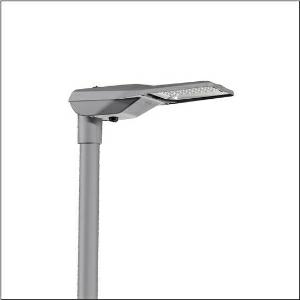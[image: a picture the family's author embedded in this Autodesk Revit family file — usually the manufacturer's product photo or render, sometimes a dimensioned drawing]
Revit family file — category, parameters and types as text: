
# Revit family: streetlight_sl_21_iq_mini___st1_0a_5xe2d21y08jb_5dbb
name_source: partatom
category: Lighting Fixtures
units: mm (PartAtom-declared; Revit-internal decimal feet)

## family parameters
Cut with Voids When Loaded = No
Host = Face
Light Source = No
Part Type = Normal
Room Calculation Point = No
Round Connector Dimension = Use Diameter
Shared = No

## types (1)
- --- (1 x LED, 9000 lm, 72.5 W, 2200K)
    Apparent Load = 73 VA
    CIE Flux Codes = 40 73 97 100 100
    Color Rendering = 70
    Color Temperature = 2200K
    Default Elevation = 1800 mm
    Description = Streetlight SL 21 iQ mini, mast luminaire, primary light control with lens, of PMMA, primary optical cover: cover, of toughened safety glass, transparent, light distribution: ST1.0a, light emission: direct distribution, primary light characteristic: asymmetric, installation type: post-top, side-entry, LED, High Power LED, rated luminous flux: 9.000lm, luminous efficacy: 124lm/W, light colour: 722, colour temperature: 2200K, control gear: iQ-Street Remote, D4i with power reduction, control: pre-setting: logarithmic dimming characteristic, Street-Remote, Auto-Match, Temp-Guard, Lumen-Switch, Night-Set, Smart-Wire, Light-Fading, Desk-Remote (wireless, voltage-free reading and setting of iQ features in the workshop via application-optimized NFC function/RFID function), optimised constant luminous flux control (CLO 2.0), mains connection: 220..240V, AC, 50/60Hz, start of lifetime: 73W, end of service life: 76W, reduction: 33W, luminaire housing, of diecast aluminium, powder-coated, Siteco® metallic grey (DB 702S), corrosivity category C5 mid according to DIN EN ISO 12944, please order mast flange separately, inclination adjustable: 0°, 5°, 10°, 15°, sealing non-destructively replaceable, multi-level sealing system, length: 628mm, width: 235mm, height: 110mm, mast flange for spigot size: 42mm (side-entry): 5XC10008XM4, 60/48mm (side-entry/post-top): 5XC10108XM2, 76/60mm (side-entry/post-top): 5XC10108XM1, mounting height: 4..8m, Smart Interface below and above, protection rating (complete): IP66, insulation class (complete): insulation class II (safety insulation), certification: CE, ENEC, ENEC+, VDE, impact resistance: IK10, permissible operating ambient temperature for outdoor applications: -40..+50°C, standard-compliant lighting for roads and squares, packaging unit: 1 piece

Light Distribution: ST1.0a
    Height = 110 mm
    Lamp = 1 x LED
    Lamp Light Flux = 9000 lm
    Lamp Power = 72.5 W
    Lamp count = 1
    Length = 625 mm
    Luminous efficacy = 124 lm/W
    Manufacturer = Siteco
    ModVariant = No
    Model = 5XE2D21Y08JB
    Number of Poles = 1
    OnlyDefault = Yes
    Power Factor = 1
    Product Name = Streetlight SL 21 iQ mini | ST1.0a
    Product group = mast luminaire | pylon top
    ProductGroupID = 6100
    Protection Class = Protection class II
    Protection Degree = IP 66
    RLX_Detail_Level = 1
    RLX_Emergency_Light_Flux = 0 lm
    RLX_Emergency_Type = 0
    RLX_Emergency_Type_DB = No
    RlxData = <blob elided: 93485 chars, md5=93a82ae1>
    Socket = socket
    Standby Power = 0 W
    System Light Flux = 9000 lm
    System Power = 73 W
    Type Comments = factory setting: luminous flux: 100 % | dim-lin: 254 | 755 mA
    Type Image = l_1003514.jpg
    URL = http://relux.com
    VarID = @adj_135625
    Voltage = 0 V
    Weight = 0.00 kg
    Width = 234 mm

## geometry (parser evidence)
native form markers: Blend x4, Sweep x12
no freeform markers — native parametric forms only
